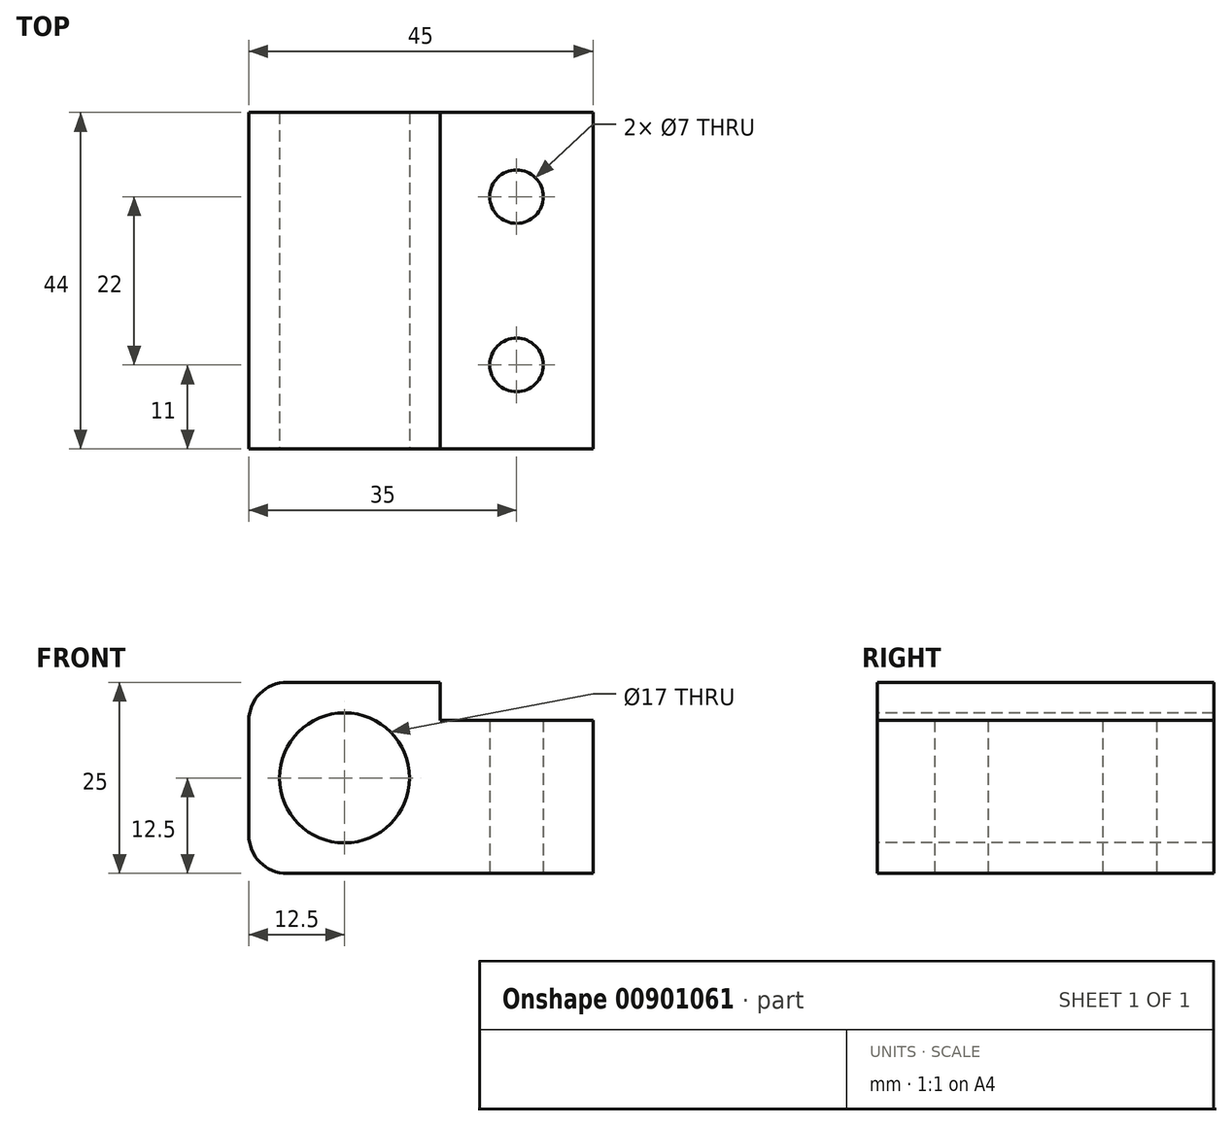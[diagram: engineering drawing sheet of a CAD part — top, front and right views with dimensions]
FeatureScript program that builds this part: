
annotation { "Feature Type Name" : "Feature", "Feature Type Description" : "" }
export const myFeature = defineFeature(function(context is Context, id is Id, definition is map)
    precondition{}
    {
        {
            var Q0;
            Q0=qCreatedBy(makeId("Top.planeOp"),FACE);
            var sketch = newSketch(context, id + "F0", { "sketchPlane" : qUnion([Q0])});
            skLineSegment(sketch, "E0.bottom", {"start": v(12.5, -22) * mm, "end": v(-12.5, -22) * mm});
            skLineSegment(sketch, "E0.top", {"start": v(12.5, 22) * mm, "end": v(-12.5, 22) * mm});
            skLineSegment(sketch, "E0.right", {"start": v(-12.5, -22) * mm, "end": v(-12.5, 22) * mm});
            skPoint(sketch, "E0.middle", {"position": v(0, 0) * mm});
            skLineSegment(sketch, "E1", {"start": v(12.5, 22) * mm, "end": v(12.5, -22) * mm});
            skLineSegment(sketch, "E2", {"start": v(12.5, -22) * mm, "end": v(32.5, -22) * mm});
            skLineSegment(sketch, "E3", {"start": v(32.5, -22) * mm, "end": v(32.5, 22) * mm});
            skLineSegment(sketch, "E4", {"start": v(32.5, 22) * mm, "end": v(12.5, 22) * mm});
            skCircle(sketch, "E5", {"center": v(22.5, 11) * mm, "radius": 3.5 * mm});
            skCircle(sketch, "E6", {"center": v(22.5, -11) * mm, "radius": 3.5 * mm});
            skSolve(sketch);
        }
        {
            var Q0;
            Q0=makeQuery(id+"F0.imprint","IMPRINT",FACE,{"disambiguationData":[TD([[makeQuery(id+"F0.imprint","IMPRINT",EDGE,{"derivedFrom":sQuery(id+"F0.wireOp",EDGE,"E0.bottom")}),-1.0]])]});
            extrude(context, id + "F1", {"entities" : qUnion([Q0]), "depth" : 25 * mm, "offsetDistance" : 25 * mm});
        }
        {
            var Q0;
            Q0=makeQuery(id+"F1.opExtrude","SWEPT_FACE",FACE,{"disambiguationData":[OSD([sQuery(id+"F0.wireOp",EDGE,"E0.bottom"),sQuery(id+"F0.wireOp",EDGE,"E2")])]});
            var sketch = newSketch(context, id + "F2", { "sketchPlane" : qUnion([Q0])});
            skCircle(sketch, "E7", {"center": v(0, 12.5) * mm, "radius": 8.5 * mm});
            skPoint(sketch, "E7.centerSnap0", {"position": v(-12.5, 12.5) * mm});
            skSolve(sketch);
        }
        {
            var Q0;
            Q0 = qSketchRegion(id + "F2", true);
            extrude(context, id + "F3", {"entities" : qUnion([Q0]), "operationType" : NewBodyOperationType.REMOVE, "endBound" : BoundingType.THROUGH_ALL, "oppositeDirection" : true, "depth" : 25 * mm, "offsetDistance" : 25 * mm});
        }
        {
            var Q0;
            Q0=makeQuery(id+"F0.imprint","IMPRINT",FACE,{"disambiguationData":[TD([[makeQuery(id+"F0.imprint","IMPRINT",EDGE,{"derivedFrom":sQuery(id+"F0.wireOp",EDGE,"E1")}),1.0]])]});
            var Q1;
            Q1=makeQuery(id+"F0.imprint","IMPRINT",FACE,{"disambiguationData":[TD([[makeQuery(id+"F0.imprint","IMPRINT",EDGE,{"derivedFrom":sQuery(id+"F0.wireOp",EDGE,"fSMG0Yw6-hnwn-Rwnt-exVP-JI2tHro1bWqK")}),-1.0]])]});
            var Q2;
            Q2=makeQuery(id+"F0.imprint","IMPRINT",FACE,{"disambiguationData":[TD([[makeQuery(id+"F0.imprint","IMPRINT",EDGE,{"derivedFrom":sQuery(id+"F0.wireOp",EDGE,"jervV3UO-4z5F-xtz5-7L9T-9r2oX97e2wMv")}),-1.0]])]});
            extrude(context, id + "F4", {"entities" : qUnion([Q0, Q1, Q2]), "operationType" : NewBodyOperationType.ADD, "depth" : 20 * mm, "offsetDistance" : 25 * mm});
        }
        {
            var Q0;
            Q0=makeQuery(id+"F1.opExtrude","CAP_EDGE",EDGE,{"disambiguationData":[OSD([sQuery(id+"F0.wireOp",EDGE,"E0.right")])],"isStart":false});
            var Q1;
            Q1=makeQuery(id+"F1.opExtrude","CAP_EDGE",EDGE,{"disambiguationData":[OSD([sQuery(id+"F0.wireOp",EDGE,"E0.right")])],"isStart":true});
            fillet(context, id + "F5", {"entities" : qUnion([Q0, Q1]), "radius" : 5 * mm, "tangentPropagation" : true, "allowEdgeOverflow" : false});
        }
    });
